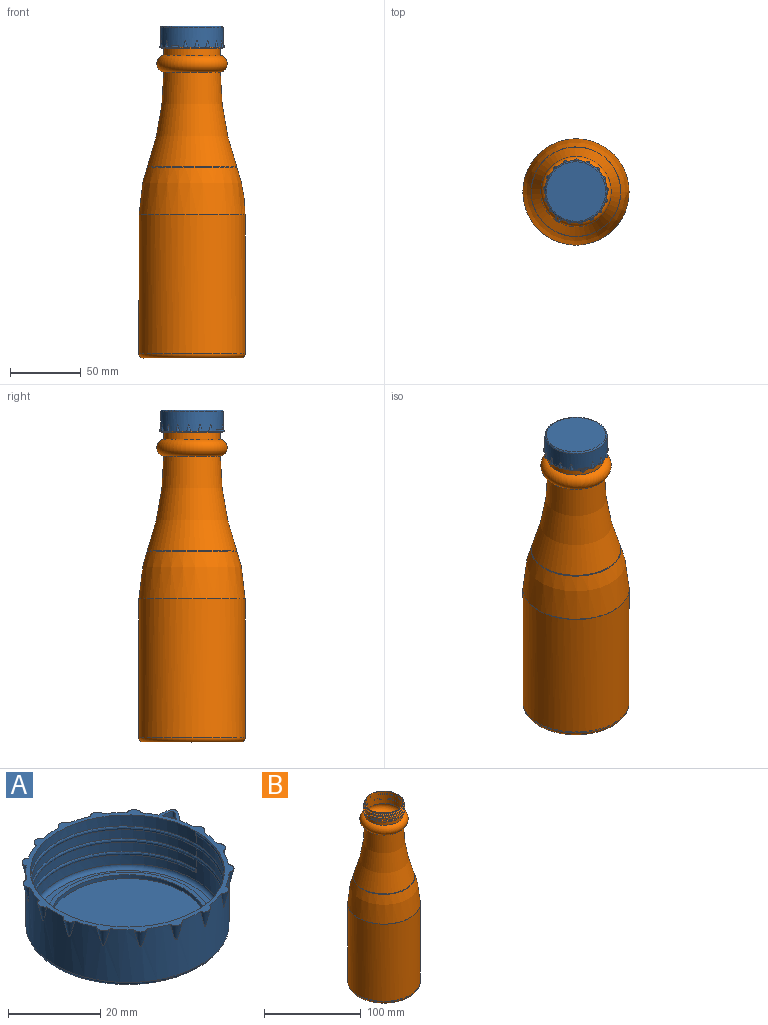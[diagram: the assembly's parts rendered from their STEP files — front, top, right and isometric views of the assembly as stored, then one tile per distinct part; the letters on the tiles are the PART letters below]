
ASSEMBLY  parts=2 mates=1
PART A: 36 faces, bbox 48.5x48.5x15 mm
  f0: cylinder r=22mm len=44mm, axis (0,0,-1), area 1802.1mm2, adj f1,f9,f17,f18,f19,f20,f21,f22
  f1: plane 47.4x45.92mm, normal (0,0,1), area 178.4mm2, adj f0,f6,f17,f18,f19,f20,f21,f22
  f2: plane 42x42mm, normal (0,0,-1), area 1385.4mm2, adj f9
  f3: cylinder r=21mm len=42mm, axis (0,0,-1), area 307.9mm2, adj f4,f6,f16
  f4: cylinder r=21mm len=42mm, axis (0,0,-1), area 307.9mm2, adj f3,f5,f16
  f5: cylinder r=21mm len=42mm, axis (0,0,-1), area 483.8mm2, adj f4,f8,f14,f16
  f6: cylinder r=21mm len=42mm, axis (0,0,-1), area 219.9mm2, adj f1,f3,f15,f16
  f7: plane 40x40mm, normal (0,0,1), area 238.8mm2, adj f8,f11
  f8: torus R=20mm, axis (0,0,1), area 203.7mm2, adj f5,f7
  f9: torus R=21mm, axis (0,0,1), area 213.5mm2, adj f0,f2
  f10: cylinder r=17mm len=34mm, axis (0,0,-1), area 106.8mm2, adj f12,f13
  f11: cylinder r=18mm len=36mm, axis (0,0,-1), area 113.1mm2, adj f7,f12
  f12: plane 36x36mm, normal (0,0,1), area 110mm2, adj f10,f11
  f13: plane 34x34mm, normal (0,0,1), area 907.9mm2, adj f10
  f14: plane 1.03x0.25mm, normal (0,-1,0), area 0.2mm2, adj f5,f16
  f15: plane 1.03x0.25mm, normal (0,1,0), area 0.2mm2, adj f6,f16
  f16: bspline ~48.5x42mm, area 443.5mm2, adj f3,f4,f5,f6,f14,f15
  f17: cone r=1.57mm half-angle=13.1deg, axis (0,0,1), area 10.4mm2, adj f0,f1
  f18: cone r=1.57mm half-angle=13.1deg, axis (0,0,1), area 10.4mm2, adj f0,f1
  f19: cone r=1.57mm half-angle=13.1deg, axis (0,0,1), area 10.4mm2, adj f0,f1
  f20: cone r=1.57mm half-angle=13.1deg, axis (0,0,1), area 10.4mm2, adj f0,f1
  f21: cone r=1.57mm half-angle=13.1deg, axis (0,0,1), area 10.4mm2, adj f0,f1
  f22: cone r=1.57mm half-angle=13.1deg, axis (0,0,1), area 10.4mm2, adj f0,f1
  f23: cone r=1.57mm half-angle=13.1deg, axis (0,0,1), area 10.4mm2, adj f0,f1
  f24: cone r=1.57mm half-angle=13.1deg, axis (0,0,1), area 10.4mm2, adj f0,f1
  f25: cone r=1.57mm half-angle=13.1deg, axis (0,0,1), area 10.4mm2, adj f0,f1
  f26: cone r=1.57mm half-angle=13.1deg, axis (0,0,1), area 10.4mm2, adj f0,f1
  f27: cone r=1.57mm half-angle=13.1deg, axis (0,0,1), area 10.4mm2, adj f0,f1
  f28: cone r=1.57mm half-angle=13.1deg, axis (0,0,1), area 10.4mm2, adj f0,f1
  f29: cone r=1.57mm half-angle=13.1deg, axis (0,0,1), area 10.4mm2, adj f0,f1
  f30: cone r=1.57mm half-angle=13.1deg, axis (0,0,1), area 10.4mm2, adj f0,f1
  f31: cone r=1.57mm half-angle=13.1deg, axis (0,0,1), area 10.4mm2, adj f0,f1
  f32: cone r=1.57mm half-angle=13.1deg, axis (0,0,1), area 10.4mm2, adj f0,f1
  f33: extruded ~4.7x3.92mm, area 12.9mm2, adj f0,f1,f35
  f34: extruded ~3.11x2.81mm, area 9mm2, adj f0,f1,f35
  f35: plane 5.08x4.96mm, normal (0,0,-1), area 5.5mm2, adj f0,f33,f34
PART B: 26 faces, bbox 168.9x168.9x344.5 mm
  f0: torus R=0.01mm, axis (0,0,1), area 3526.1mm2, adj f20
  f1: cylinder r=37mm len=97.54mm, axis (0,0,1), area 22676.8mm2, adj f2,f20
  f2: revolved ~74x74mm, area 7490.4mm2, adj f1,f3
  f3: cone r=31.25mm half-angle=19.6deg, axis (0,0,-1), area 98.5mm2, adj f2,f4
  f4: torus R=220mm, axis (0,0,1), area 10111.4mm2, adj f3,f5
  f5: torus R=18.86mm, axis (0,0,1), area 2273mm2, adj f4,f6
  f6: cylinder r=19.5mm len=39mm, axis (0,0,1), area 1890.3mm2, adj f5,f7
  f7: plane 40x40mm, normal (0,0,1), area 62mm2, adj f6,f9
  f8: cylinder r=20mm len=40mm, axis (0,0,1), area 670.2mm2, adj f9,f10,f22,f24,f25
  f9: cylinder r=20mm len=40mm, axis (0,0,1), area 209.4mm2, adj f7,f8,f23,f24
  f10: plane 43x43mm, normal (0,0,1), area 195.6mm2, adj f8,f11
  f11: cylinder r=21.5mm len=43mm, axis (0,0,1), area 202.6mm2, adj f10,f12
  f12: plane 43x43mm, normal (0,0,-1), area 195.6mm2, adj f11,f13
  f13: cylinder r=20mm len=40mm, axis (0,0,1), area 628.3mm2, adj f12,f14
  f14: torus R=18.86mm, axis (0,0,1), area 2406mm2, adj f13,f15
  f15: torus R=220mm, axis (0,0,1), area 10244.3mm2, adj f14,f16
  f16: cone r=31.72mm half-angle=19.6deg, axis (0,0,-1), area 100mm2, adj f15,f17
  f17: revolved ~75x75mm, area 7633.3mm2, adj f16,f18
  f18: cylinder r=37.5mm len=98.21mm, axis (0,0,1), area 23139.1mm2, adj f17,f21
  f19: torus R=0.01mm, axis (0,0,1), area 3632.6mm2, adj f21
  f20: torus R=34mm, axis (0,0,1), area 1236.5mm2, adj f0,f1
  f21: torus R=34.5mm, axis (0,0,-1), area 1257.3mm2, adj f18,f19
  f22: plane 1x1mm, normal (0,1,0), area 0.5mm2, adj f8,f24,f25
  f23: plane 1x1mm, normal (0,1,0), area 0.5mm2, adj f9,f24,f25
  f24: bspline ~48.5x42mm, area 273.4mm2, adj f8,f9,f22,f23,f25
  f25: bspline ~48.5x42mm, area 193.3mm2, adj f8,f22,f23,f24
PLACE A rot(axis=(0.63,-0.78,0),180deg) t=(-112.39,14.75,217.84)mm
PLACE B t=(-149.89,14.75,-17.95)mm fixed
MATE cylindrical A.f0 <-> B.f0  axis (0,0,1) through (-112.39,14.75,209.34)mm
